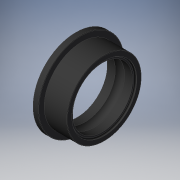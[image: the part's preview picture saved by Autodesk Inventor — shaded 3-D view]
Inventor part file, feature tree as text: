
AUTODESK INVENTOR PART (.ipt)
format: ipt  version: 2019 (Build 230136000, 136)  size: 199,680 bytes
history: native  units: mm
features: revolve x1, sketch x1
ambient origin geometry x8: Origin, YZ Plane, XZ Plane, XY Plane, X Axis, Y Axis, Z Axis, Center Point
bodies: Solid1 (feature_tree)
feature tree (2):
  revolve  "Revolution1"  [1 undecoded]
  sketch  "Sketch_21"  dims[d0=360.0deg]
note: 1 required parameter value undecoded (feature->parameter linkage not recoverable at this tier; creation-order binding heuristic only, values carry confidence <= 0.55)
